# Revit family: ERA_Вентилятор_TYPHOON
name_source: partatom
category: Оборудование
units: mm (PartAtom-declared; Revit-internal decimal feet)

## family parameters
Всегда вертикально = Да
Классификация = Нет
На основе рабочей плоскости = Нет
Общий = Нет
При загрузке вырезать с полостями = Нет
Размер круглого соединителя = Использовать диаметр
Тип детали = Вставляется
Точка расчета площади = Нет

## types (22) — shared parameters
ADSK_URL документации изделия = https://era.trade
ADSK_URL страницы изделия = https://era.trade
ADSK_Версия Revit = 2019
ADSK_Версия семейства = Ver.1 2025-02
ADSK_Единица измерения = шт.
ADSK_Завод-изготовитель = ООО «ЭРА»
ADSK_Классификация нагрузок = Электродвигатель вентилятора
ADSK_Количество = 1
ADSK_Количество фаз = 1
ADSK_Количество фаз числовое = 1
ADSK_Коэффициент мощности = 0.8
ADSK_Материал = ERA_Пластик_Серый
ADSK_Напряжение = 230 В
ADSK_Размер_Высота = 200 мм
ERA_IP вентилятора = 44
ERA_IP двигателя = 44
ERA_Гарантия = 3 года
ERA_Класс защиты = IP24
ERA_Контакты = 8 (4912) 70-16-76, 8 (4912) 24-16-00
ERA_Рабочий механизм = Осевой
ERA_Размещение = Канальное
ERA_Страна производитель = Россия
ERA_Торговая марка = ERA PRO
ERA_Управление = Механическое
ERA_Цвет = Серый
F = 216 мм
LT = ERA_Вентилятор_TYPHOON
URL = https://era.trade
h = 260 мм
Изготовитель = ООО «ЭРА»
Производитель_Контакты_Телефон = 8 (4912) 70-16-76, 8 (4912) 24-16-00

## per-type parameters (varying)
- TYPHOON 100 2SP_Скорость 1: ADSK_Код изделия=TYPHOON 100 2SP AT; ADSK_Марка=TYPHOON 100 2SP AT; ADSK_Масса=1.84; ADSK_Масса_Текст=1.84; ADSK_Наименование=Вентилятор канальный TYPHOON 100 2SP AT скорость 1; ADSK_Номинальная мощность=23 Вт; ADSK_Обозначение=TYPHOON 100 2SP AT; ADSK_Полная мощность=23 В·А; ADSK_Размер_Длина=371 мм; ADSK_Размер_Ширина=173 мм; ADSK_Ток=0 А; A_L=371 мм; B1=203 мм; B_W=173 мм; C_G=216 мм; Code1=3; D=100 мм; ERA_Опция AT (Таймер)=есть; ERA_Уровень шума=31; ERA_Частота вращения=1850; L1=40 мм; L2=61 мм; b=102 мм; Коробка_1_2_L=104 мм; Коробка_1_Vis=Да; Коробка_2_Vis=Нет; Коробка_L1=42 мм; Коробка_L2=62 мм; Коробка_W=67 мм; Лыжня_1_2_L=301 мм; Лыжня_1_2_Vis=Да; Лыжня_1_2_W=106 мм; Лыжня_1_W=14 мм; Лыжня_2_W=18 мм; Опора_Vis=Нет
- TYPHOON 100 2SP_Скорость 2: ADSK_Код изделия=TYPHOON 100 2SP AT; ADSK_Марка=TYPHOON 100 2SP AT; ADSK_Масса=1.84; ADSK_Масса_Текст=1.84; ADSK_Наименование=Вентилятор канальный TYPHOON 100 2SP AT скорость 2; ADSK_Номинальная мощность=25 Вт; ADSK_Обозначение=TYPHOON 100 2SP AT; ADSK_Полная мощность=25 В·А; ADSK_Размер_Длина=371 мм; ADSK_Размер_Ширина=173 мм; ADSK_Ток=0 А; A_L=371 мм; B1=203 мм; B_W=173 мм; C_G=216 мм; Code1=4; D=100 мм; ERA_Опция AT (Таймер)=есть; ERA_Уровень шума=40; ERA_Частота вращения=2500; L1=40 мм; L2=61 мм; b=102 мм; Коробка_1_2_L=104 мм; Коробка_1_Vis=Да; Коробка_2_Vis=Нет; Коробка_L1=42 мм; Коробка_L2=62 мм; Коробка_W=67 мм; Лыжня_1_2_L=301 мм; Лыжня_1_2_Vis=Да; Лыжня_1_2_W=106 мм; Лыжня_1_W=14 мм; Лыжня_2_W=18 мм; Опора_Vis=Нет
- TYPHOON 100 2SP AT_Скорость 1: ADSK_Код изделия=TYPHOON 100 2SP; ADSK_Марка=TYPHOON 100 2SP; ADSK_Масса=1.84; ADSK_Масса_Текст=1.84; ADSK_Наименование=Вентилятор канальный TYPHOON 100 2SP скорость 1; ADSK_Номинальная мощность=23 Вт; ADSK_Обозначение=TYPHOON 100 2SP; ADSK_Полная мощность=23 В·А; ADSK_Размер_Длина=371 мм; ADSK_Размер_Ширина=173 мм; ADSK_Ток=0 А; A_L=371 мм; B1=203 мм; B_W=173 мм; C_G=216 мм; Code1=1; D=100 мм; ERA_Опция AT (Таймер)=нет; ERA_Уровень шума=31; ERA_Частота вращения=1850; L1=40 мм; L2=61 мм; b=102 мм; Коробка_1_2_L=104 мм; Коробка_1_Vis=Да; Коробка_2_Vis=Нет; Коробка_L1=42 мм; Коробка_L2=62 мм; Коробка_W=67 мм; Лыжня_1_2_L=301 мм; Лыжня_1_2_Vis=Да; Лыжня_1_2_W=106 мм; Лыжня_1_W=14 мм; Лыжня_2_W=18 мм; Опора_Vis=Нет
- TYPHOON 100 2SP AT_Скорость 2: ADSK_Код изделия=TYPHOON 100 2SP; ADSK_Марка=TYPHOON 100 2SP; ADSK_Масса=1.84; ADSK_Масса_Текст=1.84; ADSK_Наименование=Вентилятор канальный TYPHOON 100 2SP скорость 2; ADSK_Номинальная мощность=25 Вт; ADSK_Обозначение=TYPHOON 100 2SP; ADSK_Полная мощность=25 В·А; ADSK_Размер_Длина=371 мм; ADSK_Размер_Ширина=173 мм; ADSK_Ток=0 А; A_L=371 мм; B1=203 мм; B_W=173 мм; C_G=216 мм; Code1=2; D=100 мм; ERA_Опция AT (Таймер)=нет; ERA_Уровень шума=40; ERA_Частота вращения=2500; L1=40 мм; L2=61 мм; b=102 мм; Коробка_1_2_L=104 мм; Коробка_1_Vis=Да; Коробка_2_Vis=Нет; Коробка_L1=42 мм; Коробка_L2=62 мм; Коробка_W=67 мм; Лыжня_1_2_L=301 мм; Лыжня_1_2_Vis=Да; Лыжня_1_2_W=106 мм; Лыжня_1_W=14 мм; Лыжня_2_W=18 мм; Опора_Vis=Нет
- TYPHOON 125 2SP_Скорость 1: ADSK_Код изделия=TYPHOON 125 2SP AT; ADSK_Марка=TYPHOON 125 2SP AT; ADSK_Масса=1.72; ADSK_Масса_Текст=1.72; ADSK_Наименование=Вентилятор канальный TYPHOON 125 2SP AT скорость 1; ADSK_Номинальная мощность=25 Вт; ADSK_Обозначение=TYPHOON 125 2SP AT; ADSK_Полная мощность=25 В·А; ADSK_Размер_Длина=291 мм; ADSK_Размер_Ширина=173 мм; ADSK_Ток=0 А; A_L=291 мм; B1=203 мм; B_W=173 мм; C_G=216 мм; Code1=7; D=125 мм; ERA_Опция AT (Таймер)=есть; ERA_Уровень шума=30; ERA_Частота вращения=1800; L1=40 мм; L2=61 мм; b=102 мм; Коробка_1_2_L=104 мм; Коробка_1_Vis=Да; Коробка_2_Vis=Нет; Коробка_L1=42 мм; Коробка_L2=62 мм; Коробка_W=67 мм; Лыжня_1_2_L=221 мм; Лыжня_1_2_Vis=Да; Лыжня_1_2_W=106 мм; Лыжня_1_W=14 мм; Лыжня_2_W=18 мм; Опора_Vis=Нет
- TYPHOON 125 2SP_Скорость 2: ADSK_Код изделия=TYPHOON 125 2SP AT; ADSK_Марка=TYPHOON 125 2SP AT; ADSK_Масса=1.72; ADSK_Масса_Текст=1.72; ADSK_Наименование=Вентилятор канальный TYPHOON 125 2SP AT скорость 2; ADSK_Номинальная мощность=29 Вт; ADSK_Обозначение=TYPHOON 125 2SP AT; ADSK_Полная мощность=29 В·А; ADSK_Размер_Длина=291 мм; ADSK_Размер_Ширина=173 мм; ADSK_Ток=0 А; A_L=291 мм; B1=203 мм; B_W=173 мм; C_G=216 мм; Code1=8; D=125 мм; ERA_Опция AT (Таймер)=есть; ERA_Уровень шума=39; ERA_Частота вращения=2450; L1=40 мм; L2=61 мм; b=102 мм; Коробка_1_2_L=104 мм; Коробка_1_Vis=Да; Коробка_2_Vis=Нет; Коробка_L1=42 мм; Коробка_L2=62 мм; Коробка_W=67 мм; Лыжня_1_2_L=221 мм; Лыжня_1_2_Vis=Да; Лыжня_1_2_W=106 мм; Лыжня_1_W=14 мм; Лыжня_2_W=18 мм; Опора_Vis=Нет
- TYPHOON 125 2SP AT_Скорость 1: ADSK_Код изделия=TYPHOON 125 2SP; ADSK_Марка=TYPHOON 125 2SP; ADSK_Масса=1.72; ADSK_Масса_Текст=1.72; ADSK_Наименование=Вентилятор канальный TYPHOON 125 2SP скорость 1; ADSK_Номинальная мощность=25 Вт; ADSK_Обозначение=TYPHOON 125 2SP; ADSK_Полная мощность=25 В·А; ADSK_Размер_Длина=291 мм; ADSK_Размер_Ширина=173 мм; ADSK_Ток=0 А; A_L=291 мм; B1=203 мм; B_W=173 мм; C_G=216 мм; Code1=5; D=125 мм; ERA_Опция AT (Таймер)=нет; ERA_Уровень шума=30; ERA_Частота вращения=1800; L1=40 мм; L2=61 мм; b=102 мм; Коробка_1_2_L=104 мм; Коробка_1_Vis=Да; Коробка_2_Vis=Нет; Коробка_L1=42 мм; Коробка_L2=62 мм; Коробка_W=67 мм; Лыжня_1_2_L=221 мм; Лыжня_1_2_Vis=Да; Лыжня_1_2_W=106 мм; Лыжня_1_W=14 мм; Лыжня_2_W=18 мм; Опора_Vis=Нет
- TYPHOON 125 2SP AT_Скорость 2: ADSK_Код изделия=TYPHOON 125 2SP; ADSK_Марка=TYPHOON 125 2SP; ADSK_Масса=1.72; ADSK_Масса_Текст=1.72; ADSK_Наименование=Вентилятор канальный TYPHOON 125 2SP скорость 2; ADSK_Номинальная мощность=29 Вт; ADSK_Обозначение=TYPHOON 125 2SP; ADSK_Полная мощность=29 В·А; ADSK_Размер_Длина=291 мм; ADSK_Размер_Ширина=173 мм; ADSK_Ток=0 А; A_L=291 мм; B1=203 мм; B_W=173 мм; C_G=216 мм; Code1=6; D=125 мм; ERA_Опция AT (Таймер)=нет; ERA_Уровень шума=39; ERA_Частота вращения=2450; L1=40 мм; L2=61 мм; b=102 мм; Коробка_1_2_L=104 мм; Коробка_1_Vis=Да; Коробка_2_Vis=Нет; Коробка_L1=42 мм; Коробка_L2=62 мм; Коробка_W=67 мм; Лыжня_1_2_L=221 мм; Лыжня_1_2_Vis=Да; Лыжня_1_2_W=106 мм; Лыжня_1_W=14 мм; Лыжня_2_W=18 мм; Опора_Vis=Нет
- TYPHOON 150 2SP_Скорость 1: ADSK_Код изделия=TYPHOON 150 2SP AT; ADSK_Марка=TYPHOON 150 2SP AT; ADSK_Масса=2.3; ADSK_Масса_Текст=2.3; ADSK_Наименование=Вентилятор канальный TYPHOON 150 2SP AT скорость 1; ADSK_Номинальная мощность=42 Вт; ADSK_Обозначение=TYPHOON 150 2SP AT; ADSK_Полная мощность=42 В·А; ADSK_Размер_Длина=323 мм; ADSK_Размер_Ширина=190 мм; ADSK_Ток=0 А; A_L=323 мм; B1=224 мм; B_W=190 мм; C_G=238 мм; Code1=11; D=150 мм; ERA_Опция AT (Таймер)=есть; ERA_Уровень шума=40; ERA_Частота вращения=2000; L1=47 мм; L2=70 мм; b=110 мм; Коробка_1_2_L=114 мм; Коробка_1_Vis=Да; Коробка_2_Vis=Нет; Коробка_L1=46 мм; Коробка_L2=68 мм; Коробка_W=67 мм; Лыжня_1_2_L=239 мм; Лыжня_1_2_Vis=Да; Лыжня_1_2_W=112 мм; Лыжня_1_W=15 мм; Лыжня_2_W=19 мм; Опора_Vis=Нет
- TYPHOON 150 2SP_Скорость 2: ADSK_Код изделия=TYPHOON 150 2SP AT; ADSK_Марка=TYPHOON 150 2SP AT; ADSK_Масса=2.3; ADSK_Масса_Текст=2.3; ADSK_Наименование=Вентилятор канальный TYPHOON 150 2SP AT скорость 2; ADSK_Номинальная мощность=50 Вт; ADSK_Обозначение=TYPHOON 150 2SP AT; ADSK_Полная мощность=50 В·А; ADSK_Размер_Длина=323 мм; ADSK_Размер_Ширина=190 мм; ADSK_Ток=0 А; A_L=323 мм; B1=224 мм; B_W=190 мм; C_G=238 мм; Code1=12; D=150 мм; ERA_Опция AT (Таймер)=есть; ERA_Уровень шума=49; ERA_Частота вращения=2600; L1=47 мм; L2=70 мм; b=110 мм; Коробка_1_2_L=114 мм; Коробка_1_Vis=Да; Коробка_2_Vis=Нет; Коробка_L1=46 мм; Коробка_L2=68 мм; Коробка_W=67 мм; Лыжня_1_2_L=239 мм; Лыжня_1_2_Vis=Да; Лыжня_1_2_W=112 мм; Лыжня_1_W=15 мм; Лыжня_2_W=19 мм; Опора_Vis=Нет
- TYPHOON 150 2SP AT_Скорость 1: ADSK_Код изделия=TYPHOON 150 2SP; ADSK_Марка=TYPHOON 150 2SP; ADSK_Масса=2.3; ADSK_Масса_Текст=2.3; ADSK_Наименование=Вентилятор канальный TYPHOON 150 2SP скорость 1; ADSK_Номинальная мощность=42 Вт; ADSK_Обозначение=TYPHOON 150 2SP; ADSK_Полная мощность=42 В·А; ADSK_Размер_Длина=323 мм; ADSK_Размер_Ширина=190 мм; ADSK_Ток=0 А; A_L=323 мм; B1=224 мм; B_W=190 мм; C_G=238 мм; Code1=9; D=150 мм; ERA_Опция AT (Таймер)=нет; ERA_Уровень шума=40; ERA_Частота вращения=2000; L1=47 мм; L2=70 мм; b=110 мм; Коробка_1_2_L=114 мм; Коробка_1_Vis=Да; Коробка_2_Vis=Нет; Коробка_L1=46 мм; Коробка_L2=68 мм; Коробка_W=67 мм; Лыжня_1_2_L=239 мм; Лыжня_1_2_Vis=Да; Лыжня_1_2_W=112 мм; Лыжня_1_W=15 мм; Лыжня_2_W=19 мм; Опора_Vis=Нет
- TYPHOON 150 2SP AT_Скорость 2: ADSK_Код изделия=TYPHOON 150 2SP; ADSK_Марка=TYPHOON 150 2SP; ADSK_Масса=2.3; ADSK_Масса_Текст=2.3; ADSK_Наименование=Вентилятор канальный TYPHOON 150 2SP скорость 2; ADSK_Номинальная мощность=50 Вт; ADSK_Обозначение=TYPHOON 150 2SP; ADSK_Полная мощность=50 В·А; ADSK_Размер_Длина=323 мм; ADSK_Размер_Ширина=190 мм; ADSK_Ток=0 А; A_L=323 мм; B1=224 мм; B_W=190 мм; C_G=238 мм; Code1=10; D=150 мм; ERA_Опция AT (Таймер)=нет; ERA_Уровень шума=49; ERA_Частота вращения=2600; L1=47 мм; L2=70 мм; b=110 мм; Коробка_1_2_L=114 мм; Коробка_1_Vis=Да; Коробка_2_Vis=Нет; Коробка_L1=46 мм; Коробка_L2=68 мм; Коробка_W=67 мм; Лыжня_1_2_L=239 мм; Лыжня_1_2_Vis=Да; Лыжня_1_2_W=112 мм; Лыжня_1_W=15 мм; Лыжня_2_W=19 мм; Опора_Vis=Нет
- TYPHOON 160 2SP_Скорость 1: ADSK_Код изделия=TYPHOON 160 2SP AT; ADSK_Марка=TYPHOON 160 2SP AT; ADSK_Масса=2.4; ADSK_Масса_Текст=2.4; ADSK_Наименование=Вентилятор канальный TYPHOON 160 2SP AT скорость 1; ADSK_Номинальная мощность=42 Вт; ADSK_Обозначение=TYPHOON 160 2SP AT; ADSK_Полная мощность=42 В·А; ADSK_Размер_Длина=340 мм; ADSK_Размер_Ширина=190 мм; ADSK_Ток=0 А; A_L=340 мм; B1=224 мм; B_W=190 мм; C_G=238 мм; Code1=15; D=160 мм; ERA_Опция AT (Таймер)=есть; ERA_Уровень шума=40; ERA_Частота вращения=2000; L1=51 мм; L2=97 мм; b=110 мм; Коробка_1_2_L=114 мм; Коробка_1_Vis=Да; Коробка_2_Vis=Нет; Коробка_L1=46 мм; Коробка_L2=68 мм; Коробка_W=67 мм; Лыжня_1_2_L=248 мм; Лыжня_1_2_Vis=Да; Лыжня_1_2_W=112 мм; Лыжня_1_W=17 мм; Лыжня_2_W=20 мм; Опора_Vis=Нет
- TYPHOON 160 2SP_Скорость 2: ADSK_Код изделия=TYPHOON 160 2SP AT; ADSK_Марка=TYPHOON 160 2SP AT; ADSK_Масса=2.4; ADSK_Масса_Текст=2.4; ADSK_Наименование=Вентилятор канальный TYPHOON 160 2SP AT скорость 2; ADSK_Номинальная мощность=50 Вт; ADSK_Обозначение=TYPHOON 160 2SP AT; ADSK_Полная мощность=50 В·А; ADSK_Размер_Длина=340 мм; ADSK_Размер_Ширина=190 мм; ADSK_Ток=0 А; A_L=340 мм; B1=224 мм; B_W=190 мм; C_G=238 мм; Code1=16; D=160 мм; ERA_Опция AT (Таймер)=есть; ERA_Уровень шума=49; ERA_Частота вращения=2600; L1=51 мм; L2=97 мм; b=110 мм; Коробка_1_2_L=114 мм; Коробка_1_Vis=Да; Коробка_2_Vis=Нет; Коробка_L1=46 мм; Коробка_L2=68 мм; Коробка_W=67 мм; Лыжня_1_2_L=248 мм; Лыжня_1_2_Vis=Да; Лыжня_1_2_W=112 мм; Лыжня_1_W=17 мм; Лыжня_2_W=20 мм; Опора_Vis=Нет
- TYPHOON 160 2SP AT_Скорость 1: ADSK_Код изделия=TYPHOON 160 2SP; ADSK_Марка=TYPHOON 160 2SP; ADSK_Масса=2.4; ADSK_Масса_Текст=2.4; ADSK_Наименование=Вентилятор канальный TYPHOON 160 2SP скорость 1; ADSK_Номинальная мощность=42 Вт; ADSK_Обозначение=TYPHOON 160 2SP; ADSK_Полная мощность=42 В·А; ADSK_Размер_Длина=340 мм; ADSK_Размер_Ширина=190 мм; ADSK_Ток=0 А; A_L=340 мм; B1=224 мм; B_W=190 мм; C_G=238 мм; Code1=13; D=160 мм; ERA_Опция AT (Таймер)=нет; ERA_Уровень шума=40; ERA_Частота вращения=2000; L1=51 мм; L2=97 мм; b=110 мм; Коробка_1_2_L=114 мм; Коробка_1_Vis=Да; Коробка_2_Vis=Нет; Коробка_L1=46 мм; Коробка_L2=68 мм; Коробка_W=67 мм; Лыжня_1_2_L=248 мм; Лыжня_1_2_Vis=Да; Лыжня_1_2_W=112 мм; Лыжня_1_W=17 мм; Лыжня_2_W=20 мм; Опора_Vis=Нет
- TYPHOON 160 2SP AT_Скорость 2: ADSK_Код изделия=TYPHOON 160 2SP; ADSK_Марка=TYPHOON 160 2SP; ADSK_Масса=2.4; ADSK_Масса_Текст=2.4; ADSK_Наименование=Вентилятор канальный TYPHOON 160 2SP скорость 2; ADSK_Номинальная мощность=50 Вт; ADSK_Обозначение=TYPHOON 160 2SP; ADSK_Полная мощность=50 В·А; ADSK_Размер_Длина=340 мм; ADSK_Размер_Ширина=190 мм; ADSK_Ток=0 А; A_L=340 мм; B1=224 мм; B_W=190 мм; C_G=238 мм; Code1=14; D=160 мм; ERA_Опция AT (Таймер)=нет; ERA_Уровень шума=49; ERA_Частота вращения=2600; L1=51 мм; L2=97 мм; b=110 мм; Коробка_1_2_L=114 мм; Коробка_1_Vis=Да; Коробка_2_Vis=Нет; Коробка_L1=46 мм; Коробка_L2=68 мм; Коробка_W=67 мм; Лыжня_1_2_L=248 мм; Лыжня_1_2_Vis=Да; Лыжня_1_2_W=112 мм; Лыжня_1_W=17 мм; Лыжня_2_W=20 мм; Опора_Vis=Нет
- TYPHOON 200 2SP_Скорость 1: ADSK_Код изделия=TYPHOON 200 2SP; ADSK_Марка=TYPHOON 200 2SP; ADSK_Масса=4; ADSK_Масса_Текст=4; ADSK_Наименование=Вентилятор канальный TYPHOON 200 2SP скорость 1; ADSK_Номинальная мощность=75 Вт; ADSK_Обозначение=TYPHOON 200 2SP; ADSK_Полная мощность=75 В·А; ADSK_Размер_Длина=376 мм; ADSK_Размер_Ширина=250 мм; ADSK_Ток=0 А; A_L=376 мм; B1=262 мм; B_W=250 мм; C_G=267 мм; Code1=17; D=200 мм; ERA_Опция AT (Таймер)=нет; ERA_Уровень шума=50; ERA_Частота вращения=2250; L1=33 мм; L2=38 мм; b=140 мм; Коробка_1_2_L=150 мм; Коробка_1_Vis=Да; Коробка_2_Vis=Нет; Коробка_L1=60 мм; Коробка_L2=90 мм; Коробка_W=67 мм; Лыжня_1_2_L=320 мм; Лыжня_1_2_Vis=Да; Лыжня_1_2_W=120 мм; Лыжня_1_W=18 мм; Лыжня_2_W=21 мм; Опора_Vis=Нет
- TYPHOON 200 2SP_Скорость 2: ADSK_Код изделия=TYPHOON 200 2SP; ADSK_Марка=TYPHOON 200 2SP; ADSK_Масса=4; ADSK_Масса_Текст=4; ADSK_Наименование=Вентилятор канальный TYPHOON 200 2SP скорость 2; ADSK_Номинальная мощность=105 Вт; ADSK_Обозначение=TYPHOON 200 2SP; ADSK_Полная мощность=105 В·А; ADSK_Размер_Длина=376 мм; ADSK_Размер_Ширина=250 мм; ADSK_Ток=0 А; A_L=376 мм; B1=262 мм; B_W=250 мм; C_G=267 мм; Code1=18; D=200 мм; ERA_Опция AT (Таймер)=нет; ERA_Уровень шума=58; ERA_Частота вращения=2600; L1=33 мм; L2=38 мм; b=140 мм; Коробка_1_2_L=150 мм; Коробка_1_Vis=Да; Коробка_2_Vis=Нет; Коробка_L1=60 мм; Коробка_L2=90 мм; Коробка_W=67 мм; Лыжня_1_2_L=320 мм; Лыжня_1_2_Vis=Да; Лыжня_1_2_W=120 мм; Лыжня_1_W=18 мм; Лыжня_2_W=21 мм; Опора_Vis=Нет
- TYPHOON 250 2SP_Скорость 1: ADSK_Код изделия=TYPHOON 250 2SP; ADSK_Марка=TYPHOON 250 2SP; ADSK_Масса=7.25; ADSK_Масса_Текст=7.25; ADSK_Наименование=Вентилятор канальный TYPHOON 250 2SP скорость 1; ADSK_Номинальная мощность=134 Вт; ADSK_Обозначение=TYPHOON 250 2SP; ADSK_Полная мощность=134 В·А; ADSK_Размер_Длина=455 мм; ADSK_Размер_Ширина=309 мм; ADSK_Ток=1 А; A_L=455 мм; B1=321 мм; B_W=309 мм; C_G=326 мм; Code1=19; D=250 мм; ERA_Опция AT (Таймер)=нет; ERA_Уровень шума=52; ERA_Частота вращения=1985; L1=33 мм; L2=32 мм; b=170 мм; Коробка_1_2_L=185 мм; Коробка_1_Vis=Да; Коробка_2_Vis=Нет; Коробка_L1=74 мм; Коробка_L2=111 мм; Коробка_W=67 мм; Лыжня_1_2_L=399 мм; Лыжня_1_2_Vis=Да; Лыжня_1_2_W=128 мм; Лыжня_1_W=19 мм; Лыжня_2_W=22 мм; Опора_Vis=Нет
- TYPHOON 250 2SP_Скорость 2: ADSK_Код изделия=TYPHOON 250 2SP; ADSK_Марка=TYPHOON 250 2SP; ADSK_Масса=7.25; ADSK_Масса_Текст=7.25; ADSK_Наименование=Вентилятор канальный TYPHOON 250 2SP скорость 2; ADSK_Номинальная мощность=180 Вт; ADSK_Обозначение=TYPHOON 250 2SP; ADSK_Полная мощность=180 В·А; ADSK_Размер_Длина=455 мм; ADSK_Размер_Ширина=309 мм; ADSK_Ток=1 А; A_L=455 мм; B1=321 мм; B_W=309 мм; C_G=326 мм; Code1=20; D=250 мм; ERA_Опция AT (Таймер)=нет; ERA_Уровень шума=60; ERA_Частота вращения=2550; L1=33 мм; L2=32 мм; b=170 мм; Коробка_1_2_L=185 мм; Коробка_1_Vis=Да; Коробка_2_Vis=Нет; Коробка_L1=74 мм; Коробка_L2=111 мм; Коробка_W=67 мм; Лыжня_1_2_L=399 мм; Лыжня_1_2_Vis=Да; Лыжня_1_2_W=128 мм; Лыжня_1_W=19 мм; Лыжня_2_W=22 мм; Опора_Vis=Нет
- TYPHOON 315 2SP_Скорость 1: ADSK_Код изделия=TYPHOON 315 2SP; ADSK_Марка=TYPHOON 315 2SP; ADSK_Масса=11; ADSK_Масса_Текст=11; ADSK_Наименование=Вентилятор канальный TYPHOON 315 2SP скорость 1; ADSK_Номинальная мощность=215 Вт; ADSK_Обозначение=TYPHOON 315 2SP; ADSK_Полная мощность=215 В·А; ADSK_Размер_Длина=446 мм; ADSK_Размер_Ширина=386 мм; ADSK_Ток=1 А; A_L=446 мм; B1=366 мм; B_W=386 мм; C_G=357 мм; Code1=21; D=315 мм; ERA_Опция AT (Таймер)=нет; ERA_Уровень шума=61; ERA_Частота вращения=1900; L1=56 мм; L2=65 мм; b=208 мм; Коробка_1_2_L=232 мм; Коробка_1_Vis=Нет; Коробка_2_Vis=Да; Коробка_L1=93 мм; Коробка_L2=139 мм; Коробка_W=181 мм; Лыжня_1_2_L=344 мм; Лыжня_1_2_Vis=Нет; Лыжня_1_2_W=238 мм; Лыжня_1_W=19 мм; Лыжня_2_W=22 мм; Опора_Vis=Да
- TYPHOON 315 2SP_Скорость 2: ADSK_Код изделия=TYPHOON 315 2SP; ADSK_Марка=TYPHOON 315 2SP; ADSK_Масса=11; ADSK_Масса_Текст=11; ADSK_Наименование=Вентилятор канальный TYPHOON 315 2SP скорость 2; ADSK_Номинальная мощность=285 Вт; ADSK_Обозначение=TYPHOON 315 2SP; ADSK_Полная мощность=285 В·А; ADSK_Размер_Длина=446 мм; ADSK_Размер_Ширина=386 мм; ADSK_Ток=1 А; A_L=446 мм; B1=366 мм; B_W=386 мм; C_G=357 мм; Code1=22; D=315 мм; ERA_Опция AT (Таймер)=нет; ERA_Уровень шума=69; ERA_Частота вращения=2350; L1=56 мм; L2=65 мм; b=208 мм; Коробка_1_2_L=232 мм; Коробка_1_Vis=Нет; Коробка_2_Vis=Да; Коробка_L1=93 мм; Коробка_L2=139 мм; Коробка_W=181 мм; Лыжня_1_2_L=344 мм; Лыжня_1_2_Vis=Нет; Лыжня_1_2_W=238 мм; Лыжня_1_W=19 мм; Лыжня_2_W=22 мм; Опора_Vis=Да
